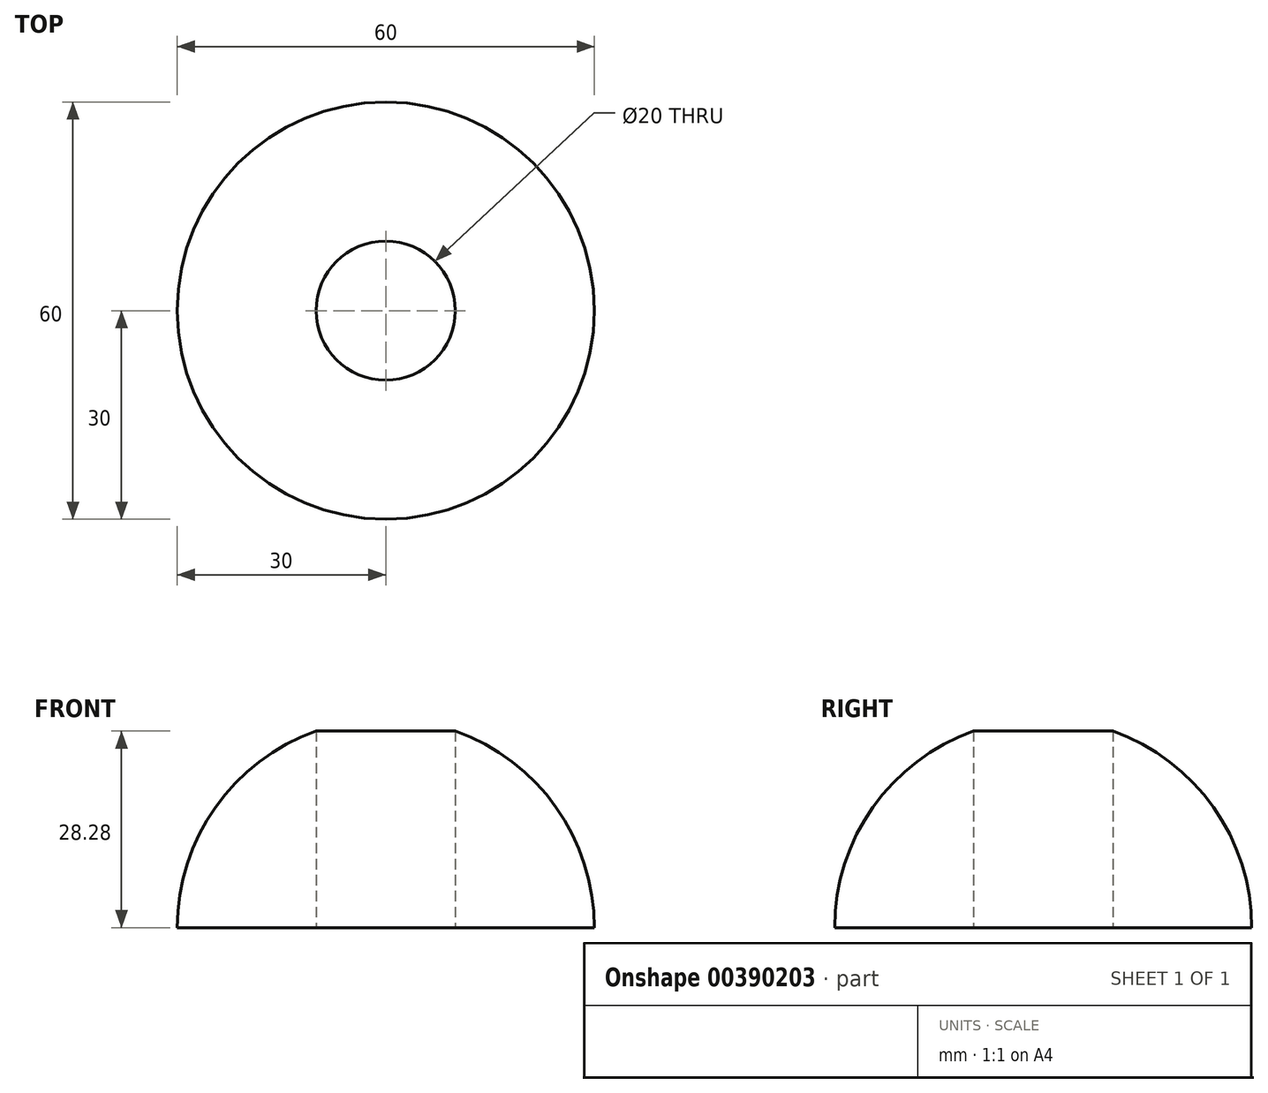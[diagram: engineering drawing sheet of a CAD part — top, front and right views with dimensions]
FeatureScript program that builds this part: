
annotation { "Feature Type Name" : "Feature", "Feature Type Description" : "" }
export const myFeature = defineFeature(function(context is Context, id is Id, definition is map)
    precondition{}
    {
        {
            var Q0;
            Q0=qCreatedBy(makeId("Top.planeOp"),FACE);
            var sketch = newSketch(context, id + "F0", { "sketchPlane" : qUnion([Q0])});
            skLineSegment(sketch, "E0", {"start": v(0, 30) * mm, "end": v(0, -30) * mm});
            skArc(sketch, "E1", {"start": v(0, 30) * mm, "mid": v(-30, 0) * mm, "end": v(0, -30) * mm});
            skSolve(sketch);
        }
        {
            var Q0;
            Q0=qCreatedBy(makeId("Front.planeOp"),FACE);
            var sketch = newSketch(context, id + "F1", { "sketchPlane" : qUnion([Q0])});
            skCircle(sketch, "E2", {"center": v(0, 0) * mm, "radius": 27.46 * mm, "construction": true});
            skSolve(sketch);
        }
        {
            var Q0;
            Q0 = qSketchRegion(id + "F0", true);
            var Q1;
            Q1=sQuery(id+"F1.wireOp",EDGE,"E2");
            revolve(context, id + "F2", {"entities" : qUnion([Q0]), "axis" : qUnion([Q1]), "revolveType" : RevolveType.FULL});
        }
        {
            var Q0;
            Q0=qCreatedBy(makeId("Front.planeOp"),FACE);
            var sketch = newSketch(context, id + "F3", { "sketchPlane" : qUnion([Q0])});
            skLineSegment(sketch, "E3", {"start": v(-30, 0) * mm, "end": v(30, 0) * mm});
            skArc(sketch, "E4", {"start": v(-30, 0) * mm, "mid": v(0, -30) * mm, "end": v(30, 0) * mm});
            skSolve(sketch);
        }
        {
            var Q0;
            Q0 = qSketchRegion(id + "F3", true);
            extrude(context, id + "F4", {"entities" : qUnion([Q0]), "operationType" : NewBodyOperationType.REMOVE, "endBound" : BoundingType.SYMMETRIC, "depth" : 60 * mm});
        }
        {
            var Q0;
            Q0=makeQuery(id+"F4.boolean.opBoolean","COPY",FACE,{"derivedFrom":makeQuery(id+"F4.opExtrude","SWEPT_FACE",FACE,{"disambiguationData":[OSD([sQuery(id+"F3.wireOp",EDGE,"E3")])]})});
            var sketch = newSketch(context, id + "F5", { "sketchPlane" : qUnion([Q0])});
            skCircle(sketch, "E5", {"center": v(0, 0) * mm, "radius": 10 * mm});
            skSolve(sketch);
        }
        {
            var Q0;
            Q0 = qSketchRegion(id + "F5", true);
            extrude(context, id + "F6", {"entities" : qUnion([Q0]), "operationType" : NewBodyOperationType.REMOVE, "oppositeDirection" : true, "depth" : 60 * mm});
        }
    });
